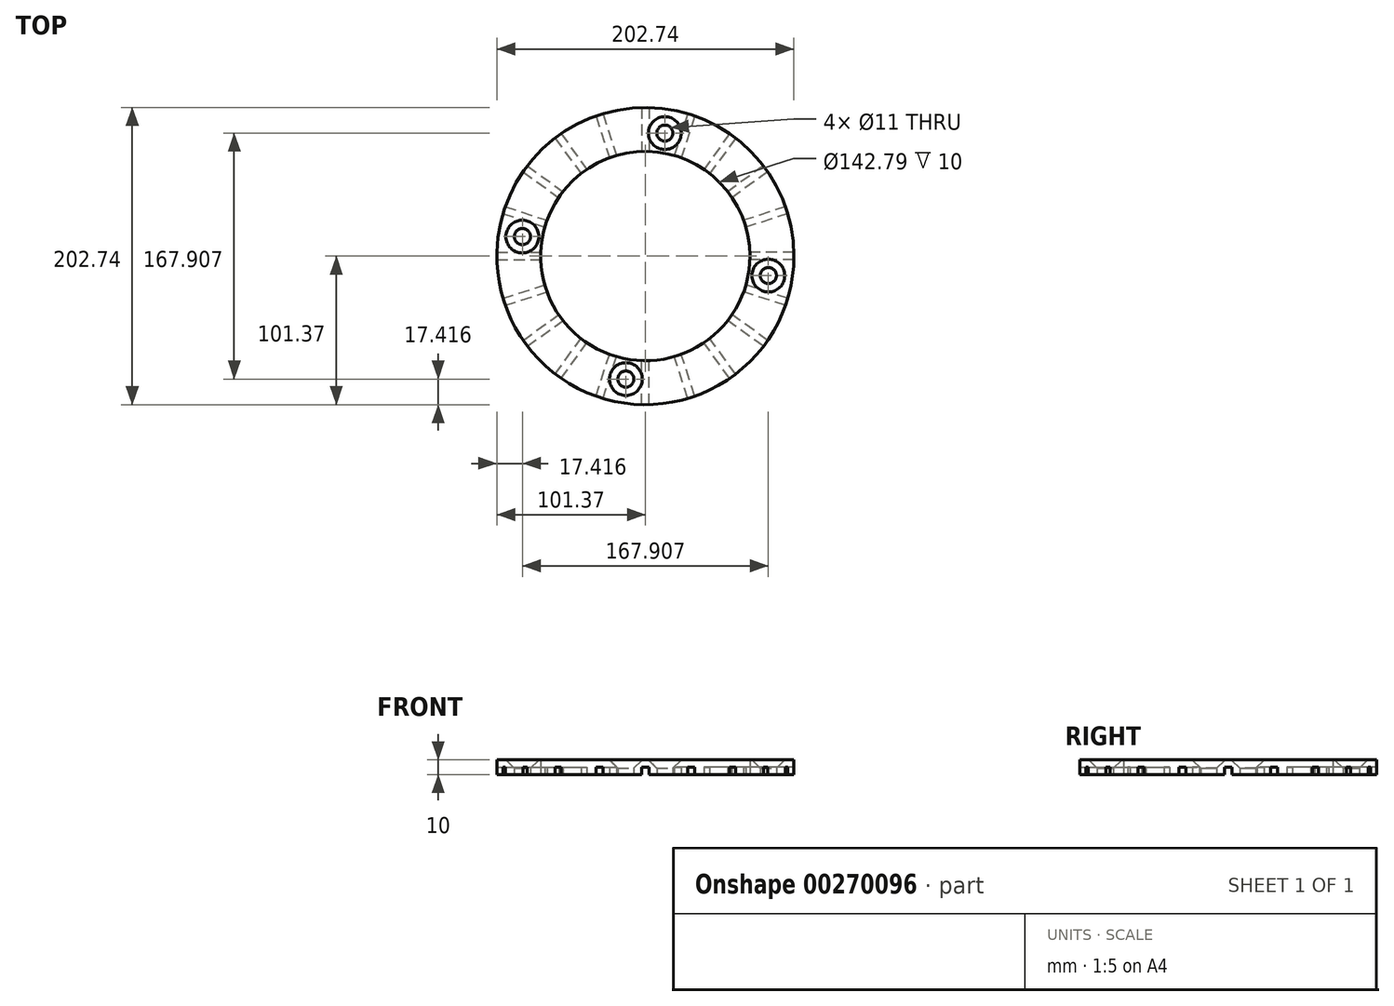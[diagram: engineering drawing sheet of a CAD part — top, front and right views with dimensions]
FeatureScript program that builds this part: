
annotation { "Feature Type Name" : "Feature", "Feature Type Description" : "" }
export const myFeature = defineFeature(function(context is Context, id is Id, definition is map)
    precondition{}
    {
        {
            var Q0;
            Q0=qCreatedBy(makeId("Top.planeOp"),FACE);
            var sketch = newSketch(context, id + "F0", { "sketchPlane" : qUnion([Q0])});
            skCircle(sketch, "E0", {"center": v(0, 0) * mm, "radius": 71.4 * mm});
            skCircle(sketch, "E1.0", {"center": v(0, 0) * mm, "radius": 101.37 * mm});
            skSolve(sketch);
        }
        {
            var Q0;
            Q0=makeQuery(id+"F0.imprint","IMPRINT",FACE,{"disambiguationData":[TD([[makeQuery(id+"F0.imprint","IMPRINT",EDGE,{"derivedFrom":sQuery(id+"F0.wireOp",EDGE,"E0")}),-1.0]])]});
            extrude(context, id + "F1", {"entities" : qUnion([Q0]), "depth" : 10 * mm});
        }
        {
            var Q0;
            Q0=makeQuery(id+"F1.opExtrude","CAP_FACE",FACE,{"disambiguationData":[OSD([sQuery(id+"F0.wireOp",EDGE,"E0"),sQuery(id+"F0.wireOp",EDGE,"E1.0")])],"isStart":true});
            var sketch = newSketch(context, id + "F2", { "sketchPlane" : qUnion([Q0])});
            skLineSegment(sketch, "E2", {"start": v(0, 134.99) * mm, "end": v(0, 0) * mm, "construction": true});
            skLineSegment(sketch, "E3.bottom", {"start": v(-2.5, 101.37) * mm, "end": v(2.5, 101.37) * mm});
            skLineSegment(sketch, "E3.left", {"start": v(-2.5, 101.37) * mm, "end": v(-2.5, 71.35) * mm});
            skLineSegment(sketch, "E3.right", {"start": v(2.5, 101.37) * mm, "end": v(2.5, 71.35) * mm});
            skPoint(sketch, "E4", {"position": v(0, 101.37) * mm});
            skPoint(sketch, "E5", {"position": v(0, 71.4) * mm});
            skLineSegment(sketch, "E6.1.0", {"start": v(-28.95, 97.18) * mm, "end": v(-19.67, 68.63) * mm});
            skLineSegment(sketch, "E6.1.1", {"start": v(-33.7, 95.64) * mm, "end": v(-28.95, 97.18) * mm});
            skLineSegment(sketch, "E6.1.2", {"start": v(-33.7, 95.64) * mm, "end": v(-24.43, 67.09) * mm});
            skLineSegment(sketch, "E6.1.3", {"start": v(-24.43, 67.09) * mm, "end": v(-19.67, 68.63) * mm});
            skLineSegment(sketch, "E6.2.0", {"start": v(-57.56, 83.48) * mm, "end": v(-39.92, 59.2) * mm});
            skLineSegment(sketch, "E6.2.1", {"start": v(-61.6, 80.54) * mm, "end": v(-57.56, 83.48) * mm});
            skLineSegment(sketch, "E6.2.2", {"start": v(-61.6, 80.54) * mm, "end": v(-43.96, 56.25) * mm});
            skLineSegment(sketch, "E6.2.3", {"start": v(-43.96, 56.25) * mm, "end": v(-39.92, 59.2) * mm});
            skLineSegment(sketch, "E6.3.0", {"start": v(-80.54, 61.6) * mm, "end": v(-56.25, 43.96) * mm});
            skLineSegment(sketch, "E6.3.1", {"start": v(-83.48, 57.56) * mm, "end": v(-80.54, 61.6) * mm});
            skLineSegment(sketch, "E6.3.2", {"start": v(-83.48, 57.56) * mm, "end": v(-59.2, 39.92) * mm});
            skLineSegment(sketch, "E6.3.3", {"start": v(-59.2, 39.92) * mm, "end": v(-56.25, 43.96) * mm});
            skLineSegment(sketch, "E6.4.0", {"start": v(-95.64, 33.7) * mm, "end": v(-67.09, 24.43) * mm});
            skLineSegment(sketch, "E6.4.1", {"start": v(-97.18, 28.95) * mm, "end": v(-95.64, 33.7) * mm});
            skLineSegment(sketch, "E6.4.2", {"start": v(-97.18, 28.95) * mm, "end": v(-68.63, 19.67) * mm});
            skLineSegment(sketch, "E6.4.3", {"start": v(-68.63, 19.67) * mm, "end": v(-67.09, 24.43) * mm});
            skLineSegment(sketch, "E6.5.0", {"start": v(-101.37, 2.5) * mm, "end": v(-71.35, 2.5) * mm});
            skLineSegment(sketch, "E6.5.1", {"start": v(-101.37, -2.5) * mm, "end": v(-101.37, 2.5) * mm});
            skLineSegment(sketch, "E6.5.2", {"start": v(-101.37, -2.5) * mm, "end": v(-71.35, -2.5) * mm});
            skLineSegment(sketch, "E6.5.3", {"start": v(-71.35, -2.5) * mm, "end": v(-71.35, 2.5) * mm});
            skLineSegment(sketch, "E6.6.0", {"start": v(-97.18, -28.95) * mm, "end": v(-68.63, -19.67) * mm});
            skLineSegment(sketch, "E6.6.1", {"start": v(-95.64, -33.7) * mm, "end": v(-97.18, -28.95) * mm});
            skLineSegment(sketch, "E6.6.2", {"start": v(-95.64, -33.7) * mm, "end": v(-67.09, -24.43) * mm});
            skLineSegment(sketch, "E6.6.3", {"start": v(-67.09, -24.43) * mm, "end": v(-68.63, -19.67) * mm});
            skLineSegment(sketch, "E6.7.0", {"start": v(-83.48, -57.56) * mm, "end": v(-59.2, -39.92) * mm});
            skLineSegment(sketch, "E6.7.1", {"start": v(-80.54, -61.6) * mm, "end": v(-83.48, -57.56) * mm});
            skLineSegment(sketch, "E6.7.2", {"start": v(-80.54, -61.6) * mm, "end": v(-56.25, -43.96) * mm});
            skLineSegment(sketch, "E6.7.3", {"start": v(-56.25, -43.96) * mm, "end": v(-59.2, -39.92) * mm});
            skLineSegment(sketch, "E6.8.0", {"start": v(-61.6, -80.54) * mm, "end": v(-43.96, -56.25) * mm});
            skLineSegment(sketch, "E6.8.1", {"start": v(-57.56, -83.48) * mm, "end": v(-61.6, -80.54) * mm});
            skLineSegment(sketch, "E6.8.2", {"start": v(-57.56, -83.48) * mm, "end": v(-39.92, -59.2) * mm});
            skLineSegment(sketch, "E6.8.3", {"start": v(-39.92, -59.2) * mm, "end": v(-43.96, -56.25) * mm});
            skLineSegment(sketch, "E6.9.0", {"start": v(-33.7, -95.64) * mm, "end": v(-24.43, -67.09) * mm});
            skLineSegment(sketch, "E6.9.1", {"start": v(-28.95, -97.18) * mm, "end": v(-33.7, -95.64) * mm});
            skLineSegment(sketch, "E6.9.2", {"start": v(-28.95, -97.18) * mm, "end": v(-19.67, -68.63) * mm});
            skLineSegment(sketch, "E6.9.3", {"start": v(-19.67, -68.63) * mm, "end": v(-24.43, -67.09) * mm});
            skLineSegment(sketch, "E6.10.0", {"start": v(-2.5, -101.37) * mm, "end": v(-2.5, -71.35) * mm});
            skLineSegment(sketch, "E6.10.1", {"start": v(2.5, -101.37) * mm, "end": v(-2.5, -101.37) * mm});
            skLineSegment(sketch, "E6.10.2", {"start": v(2.5, -101.37) * mm, "end": v(2.5, -71.35) * mm});
            skLineSegment(sketch, "E6.10.3", {"start": v(2.5, -71.35) * mm, "end": v(-2.5, -71.35) * mm});
            skLineSegment(sketch, "E6.11.0", {"start": v(28.95, -97.18) * mm, "end": v(19.67, -68.63) * mm});
            skLineSegment(sketch, "E6.11.1", {"start": v(33.7, -95.64) * mm, "end": v(28.95, -97.18) * mm});
            skLineSegment(sketch, "E6.11.2", {"start": v(33.7, -95.64) * mm, "end": v(24.43, -67.09) * mm});
            skLineSegment(sketch, "E6.11.3", {"start": v(24.43, -67.09) * mm, "end": v(19.67, -68.63) * mm});
            skLineSegment(sketch, "E6.12.0", {"start": v(57.56, -83.48) * mm, "end": v(39.92, -59.2) * mm});
            skLineSegment(sketch, "E6.12.1", {"start": v(61.6, -80.54) * mm, "end": v(57.56, -83.48) * mm});
            skLineSegment(sketch, "E6.12.2", {"start": v(61.6, -80.54) * mm, "end": v(43.96, -56.25) * mm});
            skLineSegment(sketch, "E6.12.3", {"start": v(43.96, -56.25) * mm, "end": v(39.92, -59.2) * mm});
            skLineSegment(sketch, "E6.13.0", {"start": v(80.54, -61.6) * mm, "end": v(56.25, -43.96) * mm});
            skLineSegment(sketch, "E6.13.1", {"start": v(83.48, -57.56) * mm, "end": v(80.54, -61.6) * mm});
            skLineSegment(sketch, "E6.13.2", {"start": v(83.48, -57.56) * mm, "end": v(59.2, -39.92) * mm});
            skLineSegment(sketch, "E6.13.3", {"start": v(59.2, -39.92) * mm, "end": v(56.25, -43.96) * mm});
            skLineSegment(sketch, "E6.14.0", {"start": v(95.64, -33.7) * mm, "end": v(67.09, -24.43) * mm});
            skLineSegment(sketch, "E6.14.1", {"start": v(97.18, -28.95) * mm, "end": v(95.64, -33.7) * mm});
            skLineSegment(sketch, "E6.14.2", {"start": v(97.18, -28.95) * mm, "end": v(68.63, -19.67) * mm});
            skLineSegment(sketch, "E6.14.3", {"start": v(68.63, -19.67) * mm, "end": v(67.09, -24.43) * mm});
            skLineSegment(sketch, "E6.15.0", {"start": v(101.37, -2.5) * mm, "end": v(71.35, -2.5) * mm});
            skLineSegment(sketch, "E6.15.1", {"start": v(101.37, 2.5) * mm, "end": v(101.37, -2.5) * mm});
            skLineSegment(sketch, "E6.15.2", {"start": v(101.37, 2.5) * mm, "end": v(71.35, 2.5) * mm});
            skLineSegment(sketch, "E6.15.3", {"start": v(71.35, 2.5) * mm, "end": v(71.35, -2.5) * mm});
            skLineSegment(sketch, "E6.16.0", {"start": v(97.18, 28.95) * mm, "end": v(68.63, 19.67) * mm});
            skLineSegment(sketch, "E6.16.1", {"start": v(95.64, 33.7) * mm, "end": v(97.18, 28.95) * mm});
            skLineSegment(sketch, "E6.16.2", {"start": v(95.64, 33.7) * mm, "end": v(67.09, 24.43) * mm});
            skLineSegment(sketch, "E6.16.3", {"start": v(67.09, 24.43) * mm, "end": v(68.63, 19.67) * mm});
            skLineSegment(sketch, "E6.17.0", {"start": v(83.48, 57.56) * mm, "end": v(59.2, 39.92) * mm});
            skLineSegment(sketch, "E6.17.1", {"start": v(80.54, 61.6) * mm, "end": v(83.48, 57.56) * mm});
            skLineSegment(sketch, "E6.17.2", {"start": v(80.54, 61.6) * mm, "end": v(56.25, 43.96) * mm});
            skLineSegment(sketch, "E6.17.3", {"start": v(56.25, 43.96) * mm, "end": v(59.2, 39.92) * mm});
            skLineSegment(sketch, "E6.18.0", {"start": v(61.6, 80.54) * mm, "end": v(43.96, 56.25) * mm});
            skLineSegment(sketch, "E6.18.1", {"start": v(57.56, 83.48) * mm, "end": v(61.6, 80.54) * mm});
            skLineSegment(sketch, "E6.18.2", {"start": v(57.56, 83.48) * mm, "end": v(39.92, 59.2) * mm});
            skLineSegment(sketch, "E6.18.3", {"start": v(39.92, 59.2) * mm, "end": v(43.96, 56.25) * mm});
            skLineSegment(sketch, "E6.19.0", {"start": v(33.7, 95.64) * mm, "end": v(24.43, 67.09) * mm});
            skLineSegment(sketch, "E6.19.1", {"start": v(28.95, 97.18) * mm, "end": v(33.7, 95.64) * mm});
            skLineSegment(sketch, "E6.19.2", {"start": v(28.95, 97.18) * mm, "end": v(19.67, 68.63) * mm});
            skLineSegment(sketch, "E6.19.3", {"start": v(19.67, 68.63) * mm, "end": v(24.43, 67.09) * mm});
            skPoint(sketch, "E6.center", {"position": v(0, 0) * mm});
            skLineSegment(sketch, "E7", {"start": v(-2.5, 71.35) * mm, "end": v(2.5, 71.35) * mm});
            skSolve(sketch);
        }
        {
            var Q0;
            {var subQ0=sQuery(id+"F2.wireOp",EDGE,"E7");var subQ5=sQuery(id+"F2.wireOp",EDGE,"E3.left");var subQ6=makeQuery(id+"F2.imprint","INTERSECT",VERTEX,{"derivedFrom":[subQ5,subQ0]});Q0=makeQuery(id+"F2.imprint","IMPRINT",FACE,{"disambiguationData":[TD([[makeQuery(id+"F2.imprint","IMPRINT",EDGE,{"disambiguationData":[TD([[subQ6,1.0]])],"derivedFrom":subQ5}),1.0]])]});}
            var Q1;
            {var subQ0=sQuery(id+"F2.wireOp",EDGE,"E6.19.3");var subQ1=sQuery(id+"F2.wireOp",EDGE,"E6.19.2");var subQ2=makeQuery(id+"F2.imprint","INTERSECT",VERTEX,{"derivedFrom":[subQ1,subQ0]});Q1=makeQuery(id+"F2.imprint","IMPRINT",FACE,{"disambiguationData":[TD([[makeQuery(id+"F2.imprint","IMPRINT",EDGE,{"disambiguationData":[TD([[subQ2,1.0]])],"derivedFrom":subQ1}),1.0]])]});}
            var Q2;
            {var subQ0=sQuery(id+"F2.wireOp",EDGE,"E6.18.3");var subQ1=sQuery(id+"F2.wireOp",EDGE,"E6.18.2");var subQ2=makeQuery(id+"F2.imprint","INTERSECT",VERTEX,{"derivedFrom":[subQ1,subQ0]});Q2=makeQuery(id+"F2.imprint","IMPRINT",FACE,{"disambiguationData":[TD([[makeQuery(id+"F2.imprint","IMPRINT",EDGE,{"disambiguationData":[TD([[subQ2,1.0]])],"derivedFrom":subQ1}),1.0]])]});}
            var Q3;
            {var subQ0=sQuery(id+"F2.wireOp",EDGE,"E6.17.3");var subQ1=sQuery(id+"F2.wireOp",EDGE,"E6.17.2");var subQ2=makeQuery(id+"F2.imprint","INTERSECT",VERTEX,{"derivedFrom":[subQ1,subQ0]});Q3=makeQuery(id+"F2.imprint","IMPRINT",FACE,{"disambiguationData":[TD([[makeQuery(id+"F2.imprint","IMPRINT",EDGE,{"disambiguationData":[TD([[subQ2,1.0]])],"derivedFrom":subQ1}),1.0]])]});}
            var Q4;
            {var subQ0=sQuery(id+"F2.wireOp",EDGE,"E6.16.3");var subQ5=sQuery(id+"F2.wireOp",EDGE,"E6.16.2");var subQ6=makeQuery(id+"F2.imprint","INTERSECT",VERTEX,{"derivedFrom":[subQ5,subQ0]});Q4=makeQuery(id+"F2.imprint","IMPRINT",FACE,{"disambiguationData":[TD([[makeQuery(id+"F2.imprint","IMPRINT",EDGE,{"disambiguationData":[TD([[subQ6,1.0]])],"derivedFrom":subQ5}),1.0]])]});}
            var Q5;
            {var subQ0=sQuery(id+"F2.wireOp",EDGE,"E6.15.3");var subQ1=sQuery(id+"F2.wireOp",EDGE,"E6.15.2");var subQ2=makeQuery(id+"F2.imprint","INTERSECT",VERTEX,{"derivedFrom":[subQ1,subQ0]});Q5=makeQuery(id+"F2.imprint","IMPRINT",FACE,{"disambiguationData":[TD([[makeQuery(id+"F2.imprint","IMPRINT",EDGE,{"disambiguationData":[TD([[subQ2,1.0]])],"derivedFrom":subQ1}),1.0]])]});}
            var Q6;
            {var subQ0=sQuery(id+"F2.wireOp",EDGE,"E6.14.3");var subQ5=sQuery(id+"F2.wireOp",EDGE,"E6.14.2");var subQ6=makeQuery(id+"F2.imprint","INTERSECT",VERTEX,{"derivedFrom":[subQ5,subQ0]});Q6=makeQuery(id+"F2.imprint","IMPRINT",FACE,{"disambiguationData":[TD([[makeQuery(id+"F2.imprint","IMPRINT",EDGE,{"disambiguationData":[TD([[subQ6,1.0]])],"derivedFrom":subQ5}),1.0]])]});}
            var Q7;
            {var subQ0=sQuery(id+"F2.wireOp",EDGE,"E6.13.3");var subQ5=sQuery(id+"F2.wireOp",EDGE,"E6.13.2");var subQ6=makeQuery(id+"F2.imprint","INTERSECT",VERTEX,{"derivedFrom":[subQ5,subQ0]});Q7=makeQuery(id+"F2.imprint","IMPRINT",FACE,{"disambiguationData":[TD([[makeQuery(id+"F2.imprint","IMPRINT",EDGE,{"disambiguationData":[TD([[subQ6,1.0]])],"derivedFrom":subQ5}),1.0]])]});}
            var Q8;
            {var subQ0=sQuery(id+"F2.wireOp",EDGE,"E6.12.3");var subQ1=sQuery(id+"F2.wireOp",EDGE,"E6.12.2");var subQ2=makeQuery(id+"F2.imprint","INTERSECT",VERTEX,{"derivedFrom":[subQ1,subQ0]});Q8=makeQuery(id+"F2.imprint","IMPRINT",FACE,{"disambiguationData":[TD([[makeQuery(id+"F2.imprint","IMPRINT",EDGE,{"disambiguationData":[TD([[subQ2,1.0]])],"derivedFrom":subQ1}),1.0]])]});}
            var Q9;
            {var subQ0=sQuery(id+"F2.wireOp",EDGE,"E6.11.3");var subQ1=sQuery(id+"F2.wireOp",EDGE,"E6.11.2");var subQ2=makeQuery(id+"F2.imprint","INTERSECT",VERTEX,{"derivedFrom":[subQ1,subQ0]});Q9=makeQuery(id+"F2.imprint","IMPRINT",FACE,{"disambiguationData":[TD([[makeQuery(id+"F2.imprint","IMPRINT",EDGE,{"disambiguationData":[TD([[subQ2,1.0]])],"derivedFrom":subQ1}),1.0]])]});}
            var Q10;
            {var subQ0=sQuery(id+"F2.wireOp",EDGE,"E6.10.3");var subQ5=sQuery(id+"F2.wireOp",EDGE,"E6.10.2");var subQ6=makeQuery(id+"F2.imprint","INTERSECT",VERTEX,{"derivedFrom":[subQ5,subQ0]});Q10=makeQuery(id+"F2.imprint","IMPRINT",FACE,{"disambiguationData":[TD([[makeQuery(id+"F2.imprint","IMPRINT",EDGE,{"disambiguationData":[TD([[subQ6,1.0]])],"derivedFrom":subQ5}),1.0]])]});}
            var Q11;
            {var subQ0=sQuery(id+"F2.wireOp",EDGE,"E6.9.3");var subQ5=sQuery(id+"F2.wireOp",EDGE,"E6.9.2");var subQ6=makeQuery(id+"F2.imprint","INTERSECT",VERTEX,{"derivedFrom":[subQ5,subQ0]});Q11=makeQuery(id+"F2.imprint","IMPRINT",FACE,{"disambiguationData":[TD([[makeQuery(id+"F2.imprint","IMPRINT",EDGE,{"disambiguationData":[TD([[subQ6,1.0]])],"derivedFrom":subQ5}),1.0]])]});}
            var Q12;
            {var subQ0=sQuery(id+"F2.wireOp",EDGE,"E6.8.3");var subQ5=sQuery(id+"F2.wireOp",EDGE,"E6.8.2");var subQ6=makeQuery(id+"F2.imprint","INTERSECT",VERTEX,{"derivedFrom":[subQ5,subQ0]});Q12=makeQuery(id+"F2.imprint","IMPRINT",FACE,{"disambiguationData":[TD([[makeQuery(id+"F2.imprint","IMPRINT",EDGE,{"disambiguationData":[TD([[subQ6,1.0]])],"derivedFrom":subQ5}),1.0]])]});}
            var Q13;
            {var subQ0=sQuery(id+"F2.wireOp",EDGE,"E6.7.3");var subQ5=sQuery(id+"F2.wireOp",EDGE,"E6.7.2");var subQ6=makeQuery(id+"F2.imprint","INTERSECT",VERTEX,{"derivedFrom":[subQ5,subQ0]});Q13=makeQuery(id+"F2.imprint","IMPRINT",FACE,{"disambiguationData":[TD([[makeQuery(id+"F2.imprint","IMPRINT",EDGE,{"disambiguationData":[TD([[subQ6,1.0]])],"derivedFrom":subQ5}),1.0]])]});}
            var Q14;
            {var subQ0=sQuery(id+"F2.wireOp",EDGE,"E6.6.3");var subQ5=sQuery(id+"F2.wireOp",EDGE,"E6.6.2");var subQ6=makeQuery(id+"F2.imprint","INTERSECT",VERTEX,{"derivedFrom":[subQ5,subQ0]});Q14=makeQuery(id+"F2.imprint","IMPRINT",FACE,{"disambiguationData":[TD([[makeQuery(id+"F2.imprint","IMPRINT",EDGE,{"disambiguationData":[TD([[subQ6,1.0]])],"derivedFrom":subQ5}),1.0]])]});}
            var Q15;
            {var subQ0=sQuery(id+"F2.wireOp",EDGE,"E6.5.3");var subQ7=sQuery(id+"F2.wireOp",EDGE,"E6.5.2");var subQ8=makeQuery(id+"F2.imprint","INTERSECT",VERTEX,{"derivedFrom":[subQ7,subQ0]});Q15=makeQuery(id+"F2.imprint","IMPRINT",FACE,{"disambiguationData":[TD([[makeQuery(id+"F2.imprint","IMPRINT",EDGE,{"disambiguationData":[TD([[subQ8,1.0]])],"derivedFrom":subQ7}),1.0]])]});}
            var Q16;
            {var subQ0=sQuery(id+"F2.wireOp",EDGE,"E6.4.3");var subQ1=sQuery(id+"F2.wireOp",EDGE,"E6.4.2");var subQ2=makeQuery(id+"F2.imprint","INTERSECT",VERTEX,{"derivedFrom":[subQ1,subQ0]});Q16=makeQuery(id+"F2.imprint","IMPRINT",FACE,{"disambiguationData":[TD([[makeQuery(id+"F2.imprint","IMPRINT",EDGE,{"disambiguationData":[TD([[subQ2,1.0]])],"derivedFrom":subQ1}),1.0]])]});}
            var Q17;
            {var subQ0=sQuery(id+"F2.wireOp",EDGE,"E6.3.3");var subQ5=sQuery(id+"F2.wireOp",EDGE,"E6.3.2");var subQ6=makeQuery(id+"F2.imprint","INTERSECT",VERTEX,{"derivedFrom":[subQ5,subQ0]});Q17=makeQuery(id+"F2.imprint","IMPRINT",FACE,{"disambiguationData":[TD([[makeQuery(id+"F2.imprint","IMPRINT",EDGE,{"disambiguationData":[TD([[subQ6,1.0]])],"derivedFrom":subQ5}),1.0]])]});}
            var Q18;
            {var subQ0=sQuery(id+"F2.wireOp",EDGE,"E6.2.3");var subQ5=sQuery(id+"F2.wireOp",EDGE,"E6.2.2");var subQ6=makeQuery(id+"F2.imprint","INTERSECT",VERTEX,{"derivedFrom":[subQ5,subQ0]});Q18=makeQuery(id+"F2.imprint","IMPRINT",FACE,{"disambiguationData":[TD([[makeQuery(id+"F2.imprint","IMPRINT",EDGE,{"disambiguationData":[TD([[subQ6,1.0]])],"derivedFrom":subQ5}),1.0]])]});}
            var Q19;
            {var subQ0=sQuery(id+"F2.wireOp",EDGE,"E6.1.3");var subQ5=sQuery(id+"F2.wireOp",EDGE,"E6.1.2");var subQ6=makeQuery(id+"F2.imprint","INTERSECT",VERTEX,{"derivedFrom":[subQ5,subQ0]});Q19=makeQuery(id+"F2.imprint","IMPRINT",FACE,{"disambiguationData":[TD([[makeQuery(id+"F2.imprint","IMPRINT",EDGE,{"disambiguationData":[TD([[subQ6,1.0]])],"derivedFrom":subQ5}),1.0]])]});}
            extrude(context, id + "F3", {"entities" : qUnion([Q0, Q1, Q2, Q3, Q4, Q5, Q6, Q7, Q8, Q9, Q10, Q11, Q12, Q13, Q14, Q15, Q16, Q17, Q18, Q19]), "operationType" : NewBodyOperationType.REMOVE, "oppositeDirection" : true, "depth" : 5 * mm});
        }
        {
            var Q0;
            Q0=makeQuery(id+"F1.opExtrude","CAP_FACE",FACE,{"disambiguationData":[OSD([sQuery(id+"F0.wireOp",EDGE,"E0"),sQuery(id+"F0.wireOp",EDGE,"E1.0")])],"isStart":false});
            var sketch = newSketch(context, id + "F4", { "sketchPlane" : qUnion([Q0])});
            skArc(sketch, "E8.0.0", {"start": v(97.16, 28.94) * mm, "mid": v(100.13, 15.86) * mm, "end": v(101.34, 2.5) * mm});
            skLineSegment(sketch, "E8.0.1", {"start": v(101.34, 2.5) * mm, "end": v(71.35, 2.5) * mm});
            skArc(sketch, "E8.0.2", {"start": v(71.35, 2.5) * mm, "mid": v(70.52, 11.17) * mm, "end": v(68.63, 19.67) * mm});
            skLineSegment(sketch, "E8.0.3", {"start": v(68.63, 19.67) * mm, "end": v(97.16, 28.94) * mm});
            skLineSegment(sketch, "E9.0.0", {"start": v(59.2, 39.92) * mm, "end": v(83.46, 57.55) * mm});
            skArc(sketch, "E9.0.1", {"start": v(83.46, 57.55) * mm, "mid": v(90.32, 46.02) * mm, "end": v(95.61, 33.7) * mm});
            skLineSegment(sketch, "E9.0.2", {"start": v(95.61, 33.7) * mm, "end": v(67.09, 24.43) * mm});
            skArc(sketch, "E9.0.3", {"start": v(67.09, 24.43) * mm, "mid": v(63.61, 32.41) * mm, "end": v(59.2, 39.92) * mm});
            skLineSegment(sketch, "E9.1.0", {"start": v(43.96, 56.25) * mm, "end": v(61.6, 80.52) * mm});
            skArc(sketch, "E9.1.1", {"start": v(61.6, 80.52) * mm, "mid": v(71.68, 71.68) * mm, "end": v(80.52, 61.6) * mm});
            skLineSegment(sketch, "E9.1.2", {"start": v(80.52, 61.6) * mm, "end": v(56.25, 43.96) * mm});
            skArc(sketch, "E9.1.3", {"start": v(56.25, 43.96) * mm, "mid": v(50.48, 50.48) * mm, "end": v(43.96, 56.25) * mm});
            skLineSegment(sketch, "E9.2.0", {"start": v(24.43, 67.09) * mm, "end": v(33.7, 95.61) * mm});
            skArc(sketch, "E9.2.1", {"start": v(33.7, 95.61) * mm, "mid": v(46.02, 90.32) * mm, "end": v(57.55, 83.46) * mm});
            skLineSegment(sketch, "E9.2.2", {"start": v(57.55, 83.46) * mm, "end": v(39.92, 59.2) * mm});
            skArc(sketch, "E9.2.3", {"start": v(39.92, 59.2) * mm, "mid": v(32.41, 63.61) * mm, "end": v(24.43, 67.09) * mm});
            skArc(sketch, "E9.3.0", {"start": v(2.5, 101.34) * mm, "mid": v(15.86, 100.13) * mm, "end": v(28.94, 97.16) * mm});
            skLineSegment(sketch, "E9.3.1", {"start": v(28.94, 97.16) * mm, "end": v(19.67, 68.63) * mm});
            skArc(sketch, "E9.3.2", {"start": v(19.67, 68.63) * mm, "mid": v(11.17, 70.52) * mm, "end": v(2.5, 71.35) * mm});
            skLineSegment(sketch, "E9.3.3", {"start": v(2.5, 71.35) * mm, "end": v(2.5, 101.34) * mm});
            skArc(sketch, "E9.4.0", {"start": v(-28.94, 97.16) * mm, "mid": v(-15.86, 100.13) * mm, "end": v(-2.5, 101.34) * mm});
            skLineSegment(sketch, "E9.4.1", {"start": v(-2.5, 101.34) * mm, "end": v(-2.5, 71.35) * mm});
            skArc(sketch, "E9.4.2", {"start": v(-2.5, 71.35) * mm, "mid": v(-11.17, 70.52) * mm, "end": v(-19.67, 68.63) * mm});
            skLineSegment(sketch, "E9.4.3", {"start": v(-19.67, 68.63) * mm, "end": v(-28.94, 97.16) * mm});
            skArc(sketch, "E9.5.0", {"start": v(-57.55, 83.46) * mm, "mid": v(-46.02, 90.32) * mm, "end": v(-33.7, 95.61) * mm});
            skLineSegment(sketch, "E9.5.1", {"start": v(-33.7, 95.61) * mm, "end": v(-24.43, 67.09) * mm});
            skArc(sketch, "E9.5.2", {"start": v(-24.43, 67.09) * mm, "mid": v(-32.41, 63.61) * mm, "end": v(-39.92, 59.2) * mm});
            skLineSegment(sketch, "E9.5.3", {"start": v(-39.92, 59.2) * mm, "end": v(-57.55, 83.46) * mm});
            skLineSegment(sketch, "E9.6.0", {"start": v(-56.25, 43.96) * mm, "end": v(-80.52, 61.6) * mm});
            skArc(sketch, "E9.6.1", {"start": v(-80.52, 61.6) * mm, "mid": v(-71.68, 71.68) * mm, "end": v(-61.6, 80.52) * mm});
            skLineSegment(sketch, "E9.6.2", {"start": v(-61.6, 80.52) * mm, "end": v(-43.96, 56.25) * mm});
            skArc(sketch, "E9.6.3", {"start": v(-43.96, 56.25) * mm, "mid": v(-50.48, 50.48) * mm, "end": v(-56.25, 43.96) * mm});
            skArc(sketch, "E9.7.0", {"start": v(-95.61, 33.7) * mm, "mid": v(-90.32, 46.02) * mm, "end": v(-83.46, 57.55) * mm});
            skLineSegment(sketch, "E9.7.1", {"start": v(-83.46, 57.55) * mm, "end": v(-59.2, 39.92) * mm});
            skArc(sketch, "E9.7.2", {"start": v(-59.2, 39.92) * mm, "mid": v(-63.61, 32.41) * mm, "end": v(-67.09, 24.43) * mm});
            skLineSegment(sketch, "E9.7.3", {"start": v(-67.09, 24.43) * mm, "end": v(-95.61, 33.7) * mm});
            skArc(sketch, "E9.8.0", {"start": v(-101.34, 2.5) * mm, "mid": v(-100.13, 15.86) * mm, "end": v(-97.16, 28.94) * mm});
            skLineSegment(sketch, "E9.8.1", {"start": v(-97.16, 28.94) * mm, "end": v(-68.63, 19.67) * mm});
            skArc(sketch, "E9.8.2", {"start": v(-68.63, 19.67) * mm, "mid": v(-70.52, 11.17) * mm, "end": v(-71.35, 2.5) * mm});
            skLineSegment(sketch, "E9.8.3", {"start": v(-71.35, 2.5) * mm, "end": v(-101.34, 2.5) * mm});
            skArc(sketch, "E9.9.0", {"start": v(-97.16, -28.94) * mm, "mid": v(-100.13, -15.86) * mm, "end": v(-101.34, -2.5) * mm});
            skLineSegment(sketch, "E9.9.1", {"start": v(-101.34, -2.5) * mm, "end": v(-71.35, -2.5) * mm});
            skArc(sketch, "E9.9.2", {"start": v(-71.35, -2.5) * mm, "mid": v(-70.52, -11.17) * mm, "end": v(-68.63, -19.67) * mm});
            skLineSegment(sketch, "E9.9.3", {"start": v(-68.63, -19.67) * mm, "end": v(-97.16, -28.94) * mm});
            skArc(sketch, "E9.10.0", {"start": v(-83.46, -57.55) * mm, "mid": v(-90.32, -46.02) * mm, "end": v(-95.61, -33.7) * mm});
            skLineSegment(sketch, "E9.10.1", {"start": v(-95.61, -33.7) * mm, "end": v(-67.09, -24.43) * mm});
            skArc(sketch, "E9.10.2", {"start": v(-67.09, -24.43) * mm, "mid": v(-63.61, -32.41) * mm, "end": v(-59.2, -39.92) * mm});
            skLineSegment(sketch, "E9.10.3", {"start": v(-59.2, -39.92) * mm, "end": v(-83.46, -57.55) * mm});
            skArc(sketch, "E9.11.0", {"start": v(-61.6, -80.52) * mm, "mid": v(-71.68, -71.68) * mm, "end": v(-80.52, -61.6) * mm});
            skLineSegment(sketch, "E9.11.1", {"start": v(-80.52, -61.6) * mm, "end": v(-56.25, -43.96) * mm});
            skArc(sketch, "E9.11.2", {"start": v(-56.25, -43.96) * mm, "mid": v(-50.48, -50.48) * mm, "end": v(-43.96, -56.25) * mm});
            skLineSegment(sketch, "E9.11.3", {"start": v(-43.96, -56.25) * mm, "end": v(-61.6, -80.52) * mm});
            skArc(sketch, "E9.12.0", {"start": v(-33.7, -95.61) * mm, "mid": v(-46.02, -90.32) * mm, "end": v(-57.55, -83.46) * mm});
            skLineSegment(sketch, "E9.12.1", {"start": v(-57.55, -83.46) * mm, "end": v(-39.92, -59.2) * mm});
            skArc(sketch, "E9.12.2", {"start": v(-39.92, -59.2) * mm, "mid": v(-32.41, -63.61) * mm, "end": v(-24.43, -67.09) * mm});
            skLineSegment(sketch, "E9.12.3", {"start": v(-24.43, -67.09) * mm, "end": v(-33.7, -95.61) * mm});
            skArc(sketch, "E9.13.0", {"start": v(-2.5, -101.34) * mm, "mid": v(-15.86, -100.13) * mm, "end": v(-28.94, -97.16) * mm});
            skLineSegment(sketch, "E9.13.1", {"start": v(-28.94, -97.16) * mm, "end": v(-19.67, -68.63) * mm});
            skArc(sketch, "E9.13.2", {"start": v(-19.67, -68.63) * mm, "mid": v(-11.17, -70.52) * mm, "end": v(-2.5, -71.35) * mm});
            skLineSegment(sketch, "E9.13.3", {"start": v(-2.5, -71.35) * mm, "end": v(-2.5, -101.34) * mm});
            skArc(sketch, "E9.14.0", {"start": v(28.94, -97.16) * mm, "mid": v(15.86, -100.13) * mm, "end": v(2.5, -101.34) * mm});
            skLineSegment(sketch, "E9.14.1", {"start": v(2.5, -101.34) * mm, "end": v(2.5, -71.35) * mm});
            skArc(sketch, "E9.14.2", {"start": v(2.5, -71.35) * mm, "mid": v(11.17, -70.52) * mm, "end": v(19.67, -68.63) * mm});
            skLineSegment(sketch, "E9.14.3", {"start": v(19.67, -68.63) * mm, "end": v(28.94, -97.16) * mm});
            skLineSegment(sketch, "E9.15.0", {"start": v(39.92, -59.2) * mm, "end": v(57.55, -83.46) * mm});
            skArc(sketch, "E9.15.1", {"start": v(57.55, -83.46) * mm, "mid": v(46.02, -90.32) * mm, "end": v(33.7, -95.61) * mm});
            skLineSegment(sketch, "E9.15.2", {"start": v(33.7, -95.61) * mm, "end": v(24.43, -67.09) * mm});
            skArc(sketch, "E9.15.3", {"start": v(24.43, -67.09) * mm, "mid": v(32.41, -63.61) * mm, "end": v(39.92, -59.2) * mm});
            skLineSegment(sketch, "E9.16.0", {"start": v(56.25, -43.96) * mm, "end": v(80.52, -61.6) * mm});
            skArc(sketch, "E9.16.1", {"start": v(80.52, -61.6) * mm, "mid": v(71.68, -71.68) * mm, "end": v(61.6, -80.52) * mm});
            skLineSegment(sketch, "E9.16.2", {"start": v(61.6, -80.52) * mm, "end": v(43.96, -56.25) * mm});
            skArc(sketch, "E9.16.3", {"start": v(43.96, -56.25) * mm, "mid": v(50.48, -50.48) * mm, "end": v(56.25, -43.96) * mm});
            skArc(sketch, "E9.17.0", {"start": v(95.61, -33.7) * mm, "mid": v(90.32, -46.02) * mm, "end": v(83.46, -57.55) * mm});
            skLineSegment(sketch, "E9.17.1", {"start": v(83.46, -57.55) * mm, "end": v(59.2, -39.92) * mm});
            skArc(sketch, "E9.17.2", {"start": v(59.2, -39.92) * mm, "mid": v(63.61, -32.41) * mm, "end": v(67.09, -24.43) * mm});
            skLineSegment(sketch, "E9.17.3", {"start": v(67.09, -24.43) * mm, "end": v(95.61, -33.7) * mm});
            skArc(sketch, "E9.18.0", {"start": v(101.34, -2.5) * mm, "mid": v(100.13, -15.86) * mm, "end": v(97.16, -28.94) * mm});
            skLineSegment(sketch, "E9.18.1", {"start": v(97.16, -28.94) * mm, "end": v(68.63, -19.67) * mm});
            skArc(sketch, "E9.18.2", {"start": v(68.63, -19.67) * mm, "mid": v(70.52, -11.17) * mm, "end": v(71.35, -2.5) * mm});
            skLineSegment(sketch, "E9.18.3", {"start": v(71.35, -2.5) * mm, "end": v(101.34, -2.5) * mm});
            skCircle(sketch, "E10", {"center": v(0, 0) * mm, "radius": 85 * mm, "construction": true});
            skPoint(sketch, "E11", {"position": v(13.3, 83.95) * mm});
            skLineSegment(sketch, "E12", {"start": v(0, 0) * mm, "end": v(21.79, 137.55) * mm, "construction": true});
            skLineSegment(sketch, "E13", {"start": v(-180.77, 28.63) * mm, "end": v(191.54, -30.34) * mm, "construction": true});
            skPoint(sketch, "E14", {"position": v(83.95, -13.3) * mm});
            skPoint(sketch, "E15.MirrorP", {"position": v(-13.3, -83.95) * mm});
            skPoint(sketch, "E16.MirrorP", {"position": v(-83.95, 13.3) * mm});
            skSolve(sketch);
        }
        {
            var Q0;
            Q0=sQuery(id+"F4.wireOp",VERTEX,"E11");
            var Q1;
            Q1=sQuery(id+"F4.wireOp",VERTEX,"E14");
            var Q2;
            Q2=sQuery(id+"F4.wireOp",VERTEX,"E16.MirrorP");
            var Q3;
            Q3=sQuery(id+"F4.wireOp",VERTEX,"E15.MirrorP");
            var Q4;
            Q4=makeQuery(id+"F1.opExtrude","SWEPT_BODY",BODY,{"disambiguationData":[OSD([sQuery(id+"F0.wireOp",EDGE,"E0"),sQuery(id+"F0.wireOp",EDGE,"E1.0")])]});
            hole(context, id + "F5", {"style" : HoleStyle.C_SINK, "endStyle" : HoleEndStyle.THROUGH, "standardTappedOrClearance" : lookupTablePath({ "standard" : "ISO", "fit" : "Normal", "size" : "M10", "type" : "Clearance" }), "standardBlindInLast" : lookupTablePath({ "fit" : "Standard", "standard" : "ISO", "size" : "M10", "type" : "Clearance" }), "holeDiameter" : 11 * mm, "cSinkDiameter" : 22.4 * mm, "cSinkAngle" : 90 * degree, "tappedDepth" : 12 * mm, "tapClearance" : 3, "startFromSketch" : true, "locations" : qUnion([Q0, Q1, Q2, Q3]), "scope" : qUnion([Q4])});
        }
    });
